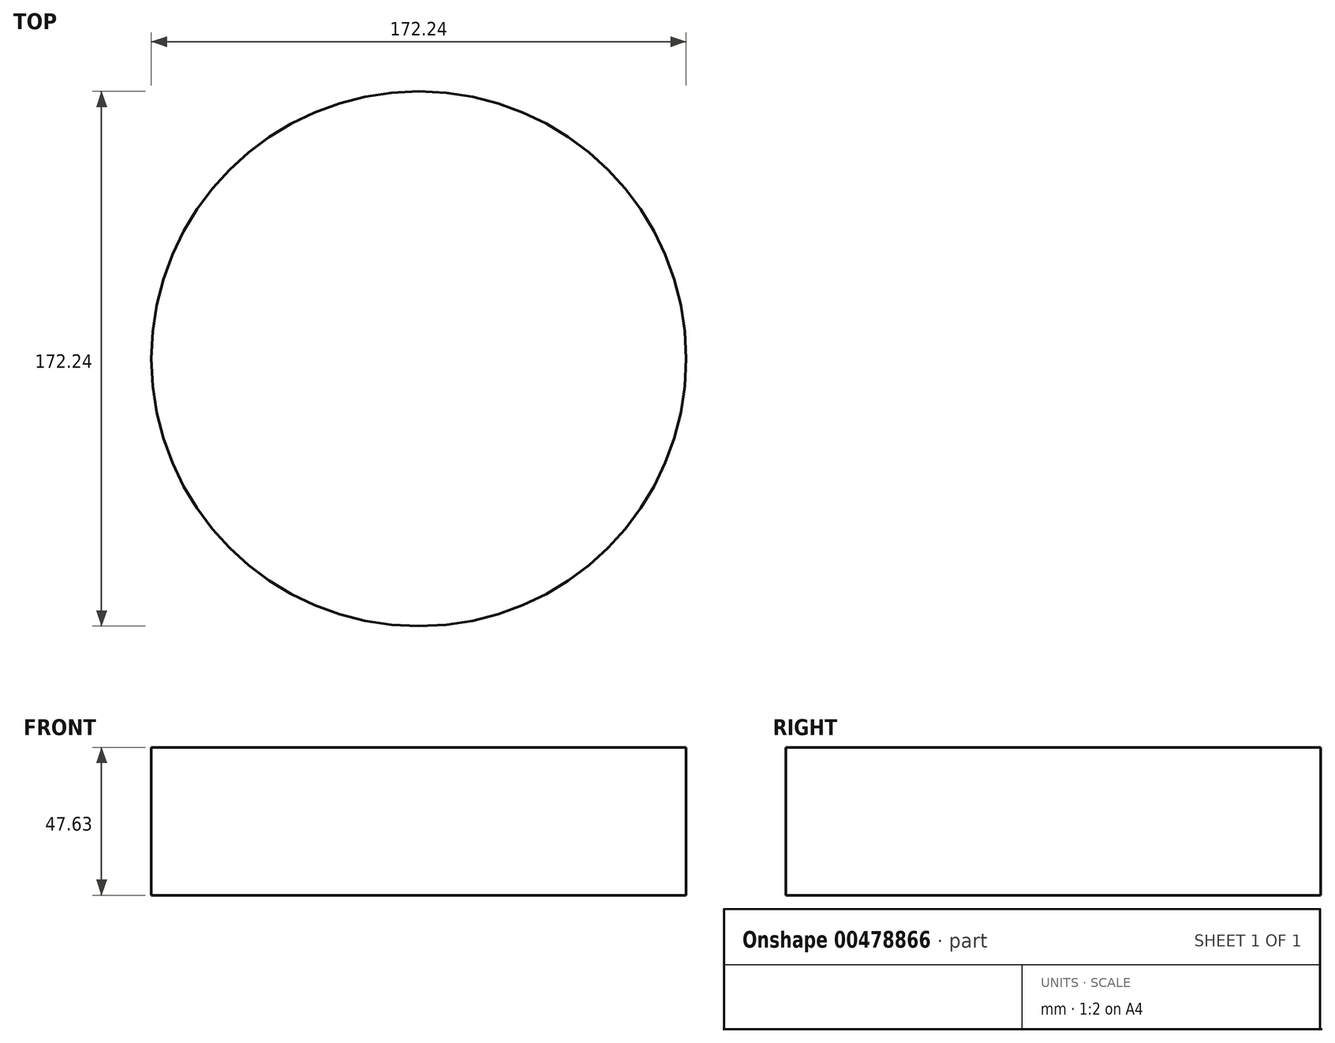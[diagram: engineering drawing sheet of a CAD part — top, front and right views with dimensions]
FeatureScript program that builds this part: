
annotation { "Feature Type Name" : "Feature", "Feature Type Description" : "" }
export const myFeature = defineFeature(function(context is Context, id is Id, definition is map)
    precondition{}
    {
        {
            var Q0;
            Q0=qCreatedBy(makeId("Top.planeOp"),FACE);
            var sketch = newSketch(context, id + "F0", { "sketchPlane" : qUnion([Q0])});
            skCircle(sketch, "E0", {"center": v(0, 0) * mm, "radius": 86.12 * mm});
            skSolve(sketch);
        }
        {
            var Q0;
            Q0=makeQuery(id+"F0.imprint","IMPRINT",FACE,{"disambiguationData":[TD([[makeQuery(id+"F0.imprint","IMPRINT",EDGE,{"derivedFrom":sQuery(id+"F0.wireOp",EDGE,"E0")}),1.0]])]});
            extrude(context, id + "F1", {"entities" : qUnion([Q0]), "depth" : 47.62 * mm});
        }
    });
